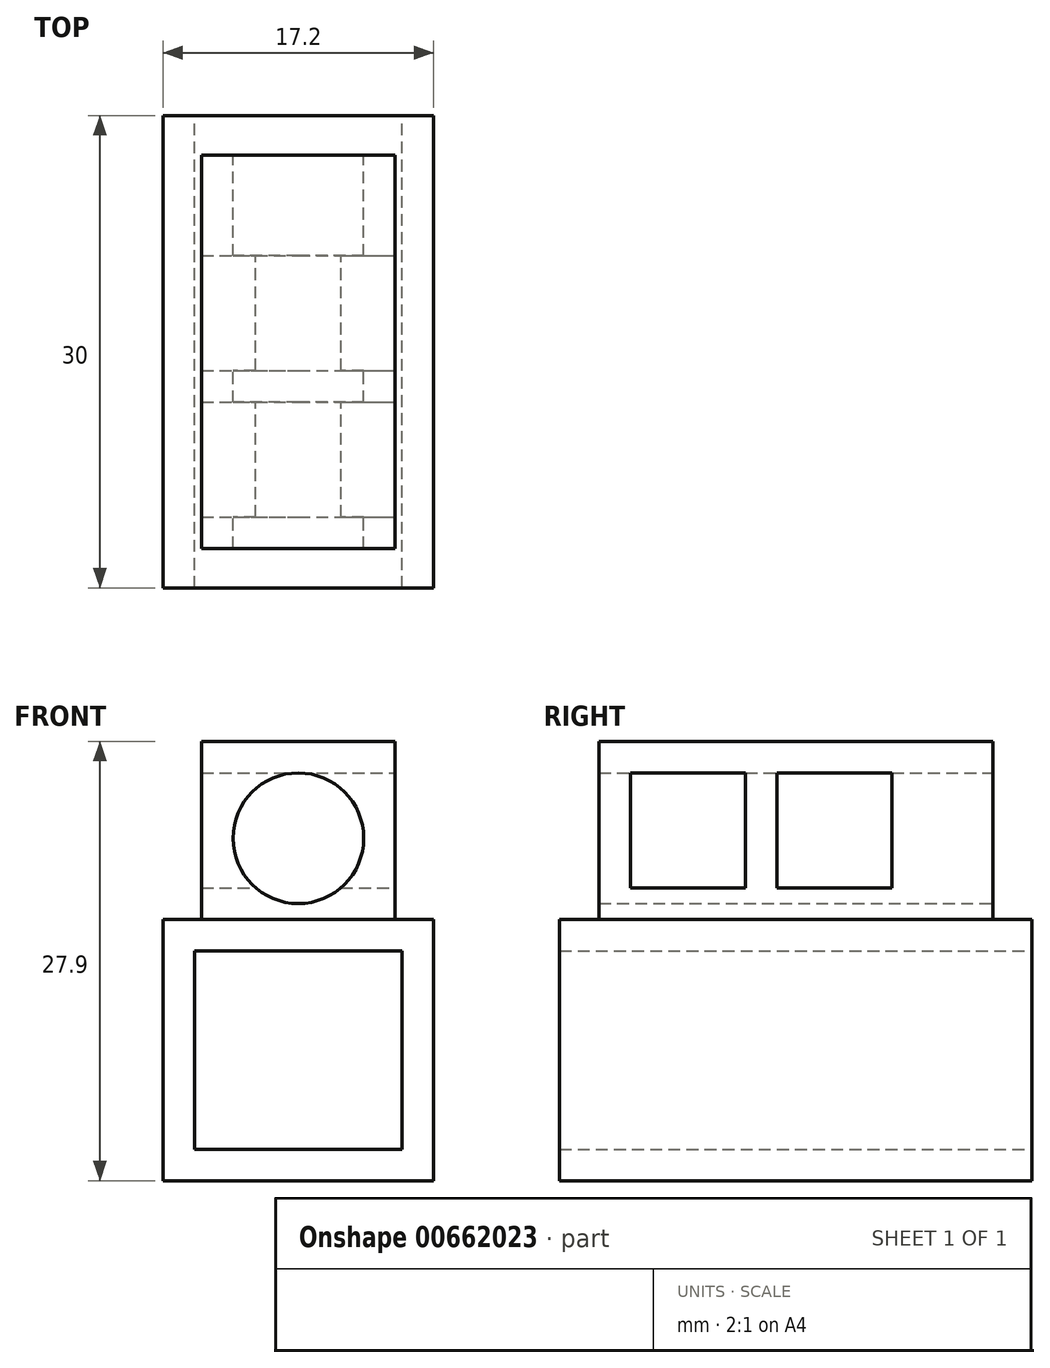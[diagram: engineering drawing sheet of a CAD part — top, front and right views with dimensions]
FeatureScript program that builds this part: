
annotation { "Feature Type Name" : "Feature", "Feature Type Description" : "" }
export const myFeature = defineFeature(function(context is Context, id is Id, definition is map)
    precondition{}
    {
        {
            var Q0;
            Q0=qCreatedBy(makeId("Front.planeOp"),FACE);
            var sketch = newSketch(context, id + "F0", { "sketchPlane" : qUnion([Q0])});
            skLineSegment(sketch, "E0.bottom", {"start": v(6.6, 6.3) * mm, "end": v(-6.6, 6.3) * mm});
            skLineSegment(sketch, "E0.top", {"start": v(6.6, -6.3) * mm, "end": v(-6.6, -6.3) * mm});
            skLineSegment(sketch, "E0.left", {"start": v(6.6, 6.3) * mm, "end": v(6.6, -6.3) * mm});
            skLineSegment(sketch, "E0.right", {"start": v(-6.6, 6.3) * mm, "end": v(-6.6, -6.3) * mm});
            skPoint(sketch, "E0.middle", {"position": v(0, 0) * mm});
            skLineSegment(sketch, "E1.0", {"start": v(8.6, 8.3) * mm, "end": v(-8.6, 8.3) * mm});
            skLineSegment(sketch, "E1.1", {"start": v(8.6, 8.3) * mm, "end": v(8.6, -8.3) * mm});
            skLineSegment(sketch, "E1.2", {"start": v(8.6, -8.3) * mm, "end": v(-8.6, -8.3) * mm});
            skLineSegment(sketch, "E1.3", {"start": v(-8.6, 8.3) * mm, "end": v(-8.6, -8.3) * mm});
            skLineSegment(sketch, "E2", {"start": v(-6.15, 19.6) * mm, "end": v(6.15, 19.6) * mm});
            skCircle(sketch, "E3", {"center": v(0, 13.45) * mm, "radius": 4.15 * mm});
            skLineSegment(sketch, "E4", {"start": v(6.15, 19.6) * mm, "end": v(6.15, 8.3) * mm});
            skLineSegment(sketch, "E5", {"start": v(-6.15, 19.6) * mm, "end": v(-6.15, 8.3) * mm});
            skSolve(sketch);
        }
        {
            var Q0;
            Q0=makeQuery(id+"F0.imprint","IMPRINT",FACE,{"disambiguationData":[TD([[makeQuery(id+"F0.imprint","IMPRINT",EDGE,{"derivedFrom":sQuery(id+"F0.wireOp",EDGE,"E0.bottom")}),-1.0]])]});
            extrude(context, id + "F1", {"entities" : qUnion([Q0]), "endBound" : BoundingType.SYMMETRIC, "depth" : 30 * mm, "offsetDistance" : 25 * mm});
        }
        {
            var Q0;
            Q0=makeQuery(id+"F0.imprint","IMPRINT",FACE,{"disambiguationData":[TD([[makeQuery(id+"F0.imprint","IMPRINT",EDGE,{"derivedFrom":sQuery(id+"F0.wireOp",EDGE,"E2")}),-1.0]])]});
            extrude(context, id + "F2", {"entities" : qUnion([Q0]), "operationType" : NewBodyOperationType.ADD, "endBound" : BoundingType.SYMMETRIC, "depth" : 25 * mm, "offsetDistance" : 25 * mm});
        }
        {
            var Q0;
            Q0=makeQuery(id+"F2.opExtrude","SWEPT_FACE",FACE,{"disambiguationData":[OSD([sQuery(id+"F0.wireOp",EDGE,"E4")])]});
            var sketch = newSketch(context, id + "F3", { "sketchPlane" : qUnion([Q0])});
            skCircle(sketch, "E6.cCircle", {"center": v(-6.85, 13.95) * mm, "radius": 3.65 * mm, "construction": true});
            skLineSegment(sketch, "E6.0", {"start": v(-10.5, 17.6) * mm, "end": v(-3.2, 17.6) * mm});
            skLineSegment(sketch, "E6.1", {"start": v(-3.2, 17.6) * mm, "end": v(-3.2, 10.3) * mm});
            skLineSegment(sketch, "E6.2", {"start": v(-3.2, 10.3) * mm, "end": v(-10.5, 10.3) * mm});
            skLineSegment(sketch, "E6.3", {"start": v(-10.5, 10.3) * mm, "end": v(-10.5, 17.6) * mm});
            skPoint(sketch, "E6.0.midPoint", {"position": v(-6.85, 17.6) * mm});
            skLineSegment(sketch, "E7", {"start": v(-12.5, 13.95) * mm, "end": v(12.5, 13.95) * mm, "construction": true});
            skCircle(sketch, "E8.cCircle", {"center": v(2.45, 13.95) * mm, "radius": 3.65 * mm, "construction": true});
            skLineSegment(sketch, "E8.0", {"start": v(6.1, 17.6) * mm, "end": v(6.1, 10.3) * mm});
            skLineSegment(sketch, "E8.1", {"start": v(6.1, 10.3) * mm, "end": v(-1.2, 10.3) * mm});
            skLineSegment(sketch, "E8.2", {"start": v(-1.2, 10.3) * mm, "end": v(-1.2, 17.6) * mm});
            skLineSegment(sketch, "E8.3", {"start": v(-1.2, 17.6) * mm, "end": v(6.1, 17.6) * mm});
            skPoint(sketch, "E8.0.midPoint", {"position": v(6.1, 13.95) * mm});
            skSolve(sketch);
        }
        {
            var Q0;
            Q0 = qSketchRegion(id + "F3", true);
            extrude(context, id + "F4", {"entities" : qUnion([Q0]), "operationType" : NewBodyOperationType.REMOVE, "oppositeDirection" : true, "depth" : 25 * mm, "offsetDistance" : 25 * mm});
        }
    });
